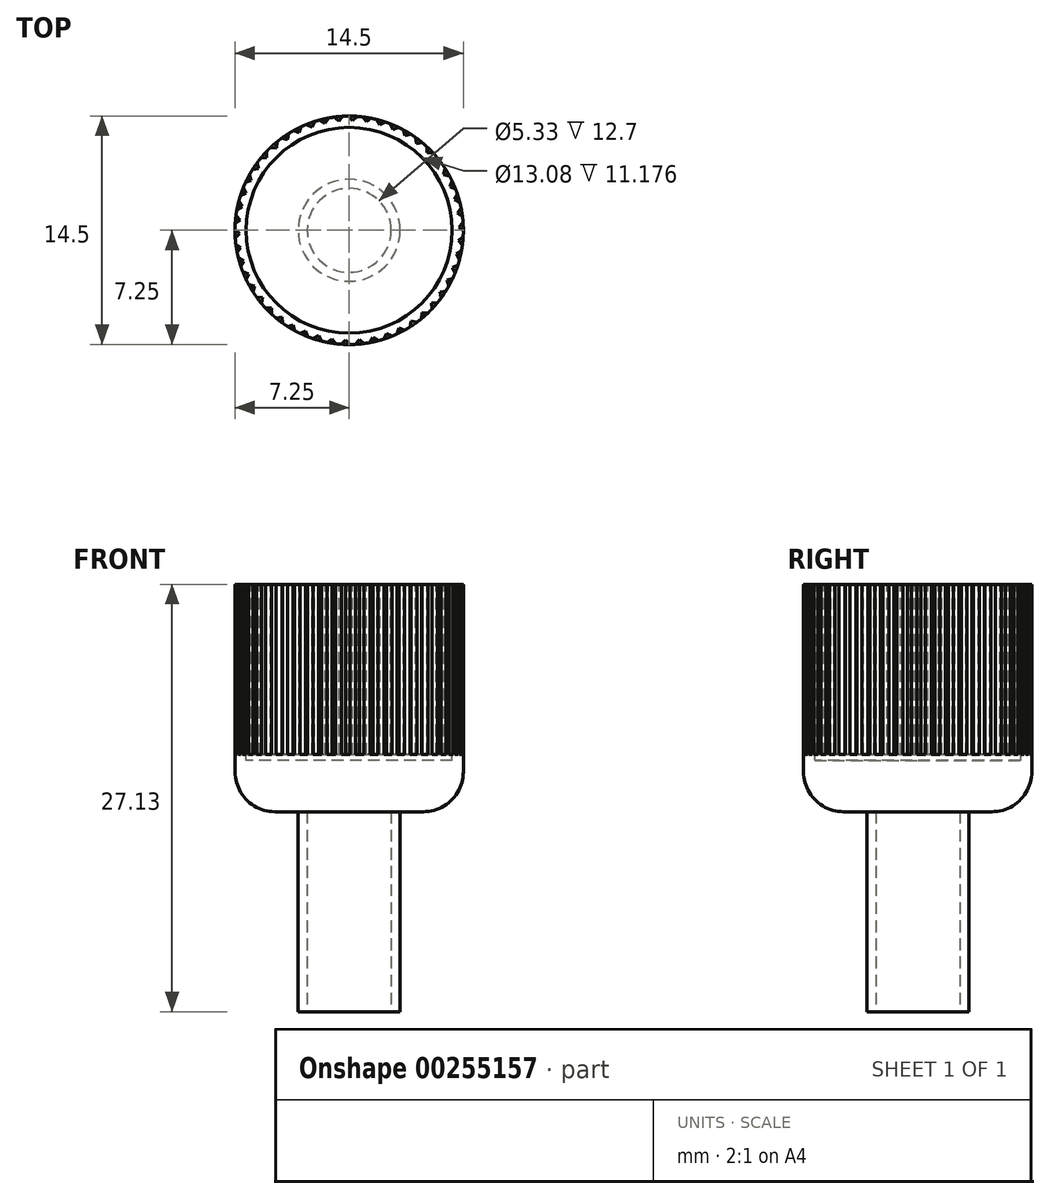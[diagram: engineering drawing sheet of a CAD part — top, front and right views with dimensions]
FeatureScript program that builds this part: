
annotation { "Feature Type Name" : "Feature", "Feature Type Description" : "" }
export const myFeature = defineFeature(function(context is Context, id is Id, definition is map)
    precondition{}
    {
        {
            var Q0;
            Q0=qCreatedBy(makeId("Top.planeOp"),FACE);
            var sketch = newSketch(context, id + "F0", { "sketchPlane" : qUnion([Q0])});
            skCircle(sketch, "E0", {"center": v(0, 0) * mm, "radius": 3.24 * mm});
            skCircle(sketch, "E1", {"center": v(0, 0) * mm, "radius": 2.67 * mm});
            skSolve(sketch);
        }
        {
            var Q0;
            Q0=makeQuery(id+"F0.imprint","IMPRINT",FACE,{"disambiguationData":[TD([[makeQuery(id+"F0.imprint","IMPRINT",EDGE,{"derivedFrom":sQuery(id+"F0.wireOp",EDGE,"E0")}),1.0]])]});
            extrude(context, id + "F1", {"entities" : qUnion([Q0]), "depth" : 12.7 * mm});
        }
        {
            var Q0;
            Q0=makeQuery(id+"F1.opExtrude","CAP_FACE",FACE,{"disambiguationData":[OSD([sQuery(id+"F0.wireOp",EDGE,"E0"),sQuery(id+"F0.wireOp",EDGE,"E1")])],"isStart":false});
            var sketch = newSketch(context, id + "F2", { "sketchPlane" : qUnion([Q0])});
            skCircle(sketch, "E2", {"center": v(0, 0) * mm, "radius": 7.25 * mm});
            skSolve(sketch);
        }
        {
            var Q0;
            Q0 = qSketchRegion(id + "F2", true);
            extrude(context, id + "F3", {"entities" : qUnion([Q0]), "operationType" : NewBodyOperationType.ADD, "depth" : 14.43 * mm});
        }
        {
            var Q0;
            Q0=makeQuery(id+"F3.opExtrude","CAP_EDGE",EDGE,{"disambiguationData":[OSD([sQuery(id+"F2.wireOp",EDGE,"E2")])],"isStart":true});
            fillet(context, id + "F4", {"entities" : qUnion([Q0]), "radius" : 2.54 * mm, "tangentPropagation" : true, "allowEdgeOverflow" : false});
        }
        {
            var Q0;
            Q0=makeQuery(id+"F3.opExtrude","CAP_FACE",FACE,{"disambiguationData":[OSD([sQuery(id+"F2.wireOp",EDGE,"E2")])],"isStart":false});
            var sketch = newSketch(context, id + "F5", { "sketchPlane" : qUnion([Q0])});
            skCircle(sketch, "E3", {"center": v(0, 0) * mm, "radius": 6.54 * mm});
            skSolve(sketch);
        }
        {
            var Q0;
            Q0=makeQuery(id+"F5.imprint","IMPRINT",FACE,{"disambiguationData":[TD([[makeQuery(id+"F5.imprint","IMPRINT",EDGE,{"derivedFrom":sQuery(id+"F5.wireOp",EDGE,"E3")}),1.0]])]});
            extrude(context, id + "F6", {"entities" : qUnion([Q0]), "operationType" : NewBodyOperationType.REMOVE, "oppositeDirection" : true, "depth" : 11.18 * mm});
        }
        {
            var Q0;
            Q0=makeQuery(id+"F3.opExtrude","CAP_FACE",FACE,{"disambiguationData":[OSD([sQuery(id+"F2.wireOp",EDGE,"E2")])],"isStart":false});
            var sketch = newSketch(context, id + "F7", { "sketchPlane" : qUnion([Q0])});
            skLineSegment(sketch, "E4", {"start": v(4.93, 5.31) * mm, "end": v(4.93, 4.93) * mm});
            skLineSegment(sketch, "E5", {"start": v(4.93, 4.93) * mm, "end": v(5.31, 4.93) * mm});
            skArc(sketch, "E6.0", {"start": v(5.9, 4.23) * mm, "mid": v(5.44, 4.8) * mm, "end": v(4.93, 5.31) * mm});
            skLineSegment(sketch, "E7.1.0", {"start": v(4.23, 5.9) * mm, "end": v(4.28, 5.51) * mm});
            skLineSegment(sketch, "E7.1.1", {"start": v(4.28, 5.51) * mm, "end": v(4.65, 5.56) * mm});
            skLineSegment(sketch, "E7.2.0", {"start": v(3.46, 6.37) * mm, "end": v(3.55, 6) * mm});
            skLineSegment(sketch, "E7.2.1", {"start": v(3.55, 6) * mm, "end": v(3.92, 6.1) * mm});
            skLineSegment(sketch, "E7.3.0", {"start": v(2.63, 6.76) * mm, "end": v(2.77, 6.4) * mm});
            skLineSegment(sketch, "E7.3.1", {"start": v(2.77, 6.4) * mm, "end": v(3.13, 6.54) * mm});
            skLineSegment(sketch, "E7.4.0", {"start": v(1.76, 7.03) * mm, "end": v(1.95, 6.7) * mm});
            skLineSegment(sketch, "E7.4.1", {"start": v(1.95, 6.7) * mm, "end": v(2.28, 6.88) * mm});
            skLineSegment(sketch, "E7.5.0", {"start": v(0.87, 7.2) * mm, "end": v(1.1, 6.9) * mm});
            skLineSegment(sketch, "E7.5.1", {"start": v(1.1, 6.9) * mm, "end": v(1.4, 7.12) * mm});
            skLineSegment(sketch, "E7.6.0", {"start": v(-0.04, 7.25) * mm, "end": v(0.22, 6.97) * mm});
            skLineSegment(sketch, "E7.6.1", {"start": v(0.22, 6.97) * mm, "end": v(0.5, 7.23) * mm});
            skLineSegment(sketch, "E7.7.0", {"start": v(-0.95, 7.19) * mm, "end": v(-0.66, 6.95) * mm});
            skLineSegment(sketch, "E7.7.1", {"start": v(-0.66, 6.95) * mm, "end": v(-0.41, 7.24) * mm});
            skLineSegment(sketch, "E7.8.0", {"start": v(-1.84, 7.01) * mm, "end": v(-1.52, 6.8) * mm});
            skLineSegment(sketch, "E7.8.1", {"start": v(-1.52, 6.8) * mm, "end": v(-1.32, 7.13) * mm});
            skLineSegment(sketch, "E7.9.0", {"start": v(-2.7, 6.73) * mm, "end": v(-2.36, 6.56) * mm});
            skLineSegment(sketch, "E7.9.1", {"start": v(-2.36, 6.56) * mm, "end": v(-2.2, 6.9) * mm});
            skLineSegment(sketch, "E7.10.0", {"start": v(-3.53, 6.33) * mm, "end": v(-3.17, 6.22) * mm});
            skLineSegment(sketch, "E7.10.1", {"start": v(-3.17, 6.22) * mm, "end": v(-3.05, 6.58) * mm});
            skLineSegment(sketch, "E7.11.0", {"start": v(-4.3, 5.84) * mm, "end": v(-3.92, 5.77) * mm});
            skLineSegment(sketch, "E7.11.1", {"start": v(-3.92, 5.77) * mm, "end": v(-3.85, 6.15) * mm});
            skLineSegment(sketch, "E7.12.0", {"start": v(-5, 5.26) * mm, "end": v(-4.61, 5.23) * mm});
            skLineSegment(sketch, "E7.12.1", {"start": v(-4.61, 5.23) * mm, "end": v(-4.6, 5.61) * mm});
            skLineSegment(sketch, "E7.13.0", {"start": v(-5.61, 4.6) * mm, "end": v(-5.23, 4.61) * mm});
            skLineSegment(sketch, "E7.13.1", {"start": v(-5.23, 4.61) * mm, "end": v(-5.26, 5) * mm});
            skLineSegment(sketch, "E7.14.0", {"start": v(-6.15, 3.85) * mm, "end": v(-5.77, 3.92) * mm});
            skLineSegment(sketch, "E7.14.1", {"start": v(-5.77, 3.92) * mm, "end": v(-5.84, 4.3) * mm});
            skLineSegment(sketch, "E7.15.0", {"start": v(-6.58, 3.05) * mm, "end": v(-6.22, 3.17) * mm});
            skLineSegment(sketch, "E7.15.1", {"start": v(-6.22, 3.17) * mm, "end": v(-6.33, 3.53) * mm});
            skLineSegment(sketch, "E7.16.0", {"start": v(-6.9, 2.2) * mm, "end": v(-6.56, 2.36) * mm});
            skLineSegment(sketch, "E7.16.1", {"start": v(-6.56, 2.36) * mm, "end": v(-6.73, 2.7) * mm});
            skLineSegment(sketch, "E7.17.0", {"start": v(-7.13, 1.32) * mm, "end": v(-6.8, 1.52) * mm});
            skLineSegment(sketch, "E7.17.1", {"start": v(-6.8, 1.52) * mm, "end": v(-7.01, 1.84) * mm});
            skLineSegment(sketch, "E7.18.0", {"start": v(-7.24, 0.41) * mm, "end": v(-6.95, 0.66) * mm});
            skLineSegment(sketch, "E7.18.1", {"start": v(-6.95, 0.66) * mm, "end": v(-7.19, 0.95) * mm});
            skLineSegment(sketch, "E7.19.0", {"start": v(-7.23, -0.5) * mm, "end": v(-6.97, -0.22) * mm});
            skLineSegment(sketch, "E7.19.1", {"start": v(-6.97, -0.22) * mm, "end": v(-7.25, 0.04) * mm});
            skLineSegment(sketch, "E7.20.0", {"start": v(-7.12, -1.4) * mm, "end": v(-6.9, -1.1) * mm});
            skLineSegment(sketch, "E7.20.1", {"start": v(-6.9, -1.1) * mm, "end": v(-7.2, -0.87) * mm});
            skLineSegment(sketch, "E7.21.0", {"start": v(-6.88, -2.28) * mm, "end": v(-6.7, -1.95) * mm});
            skLineSegment(sketch, "E7.21.1", {"start": v(-6.7, -1.95) * mm, "end": v(-7.03, -1.76) * mm});
            skLineSegment(sketch, "E7.22.0", {"start": v(-6.54, -3.13) * mm, "end": v(-6.4, -2.77) * mm});
            skLineSegment(sketch, "E7.22.1", {"start": v(-6.4, -2.77) * mm, "end": v(-6.76, -2.63) * mm});
            skLineSegment(sketch, "E7.23.0", {"start": v(-6.1, -3.92) * mm, "end": v(-6, -3.55) * mm});
            skLineSegment(sketch, "E7.23.1", {"start": v(-6, -3.55) * mm, "end": v(-6.37, -3.46) * mm});
            skLineSegment(sketch, "E7.24.0", {"start": v(-5.56, -4.65) * mm, "end": v(-5.51, -4.28) * mm});
            skLineSegment(sketch, "E7.24.1", {"start": v(-5.51, -4.28) * mm, "end": v(-5.9, -4.23) * mm});
            skLineSegment(sketch, "E7.25.0", {"start": v(-4.93, -5.31) * mm, "end": v(-4.93, -4.93) * mm});
            skLineSegment(sketch, "E7.25.1", {"start": v(-4.93, -4.93) * mm, "end": v(-5.31, -4.93) * mm});
            skLineSegment(sketch, "E7.26.0", {"start": v(-4.23, -5.9) * mm, "end": v(-4.28, -5.51) * mm});
            skLineSegment(sketch, "E7.26.1", {"start": v(-4.28, -5.51) * mm, "end": v(-4.65, -5.56) * mm});
            skLineSegment(sketch, "E7.27.0", {"start": v(-3.46, -6.37) * mm, "end": v(-3.55, -6) * mm});
            skLineSegment(sketch, "E7.27.1", {"start": v(-3.55, -6) * mm, "end": v(-3.92, -6.1) * mm});
            skLineSegment(sketch, "E7.28.0", {"start": v(-2.63, -6.76) * mm, "end": v(-2.77, -6.4) * mm});
            skLineSegment(sketch, "E7.28.1", {"start": v(-2.77, -6.4) * mm, "end": v(-3.13, -6.54) * mm});
            skLineSegment(sketch, "E7.29.0", {"start": v(-1.76, -7.03) * mm, "end": v(-1.95, -6.7) * mm});
            skLineSegment(sketch, "E7.29.1", {"start": v(-1.95, -6.7) * mm, "end": v(-2.28, -6.88) * mm});
            skLineSegment(sketch, "E7.30.0", {"start": v(-0.87, -7.2) * mm, "end": v(-1.1, -6.9) * mm});
            skLineSegment(sketch, "E7.30.1", {"start": v(-1.1, -6.9) * mm, "end": v(-1.4, -7.12) * mm});
            skLineSegment(sketch, "E7.31.0", {"start": v(0.04, -7.25) * mm, "end": v(-0.22, -6.97) * mm});
            skLineSegment(sketch, "E7.31.1", {"start": v(-0.22, -6.97) * mm, "end": v(-0.5, -7.23) * mm});
            skLineSegment(sketch, "E7.32.0", {"start": v(0.95, -7.19) * mm, "end": v(0.66, -6.95) * mm});
            skLineSegment(sketch, "E7.32.1", {"start": v(0.66, -6.95) * mm, "end": v(0.41, -7.24) * mm});
            skLineSegment(sketch, "E7.33.0", {"start": v(1.84, -7.01) * mm, "end": v(1.52, -6.8) * mm});
            skLineSegment(sketch, "E7.33.1", {"start": v(1.52, -6.8) * mm, "end": v(1.32, -7.13) * mm});
            skLineSegment(sketch, "E7.34.0", {"start": v(2.7, -6.73) * mm, "end": v(2.36, -6.56) * mm});
            skLineSegment(sketch, "E7.34.1", {"start": v(2.36, -6.56) * mm, "end": v(2.2, -6.9) * mm});
            skLineSegment(sketch, "E7.35.0", {"start": v(3.53, -6.33) * mm, "end": v(3.17, -6.22) * mm});
            skLineSegment(sketch, "E7.35.1", {"start": v(3.17, -6.22) * mm, "end": v(3.05, -6.58) * mm});
            skLineSegment(sketch, "E7.36.0", {"start": v(4.3, -5.84) * mm, "end": v(3.92, -5.77) * mm});
            skLineSegment(sketch, "E7.36.1", {"start": v(3.92, -5.77) * mm, "end": v(3.85, -6.15) * mm});
            skLineSegment(sketch, "E7.37.0", {"start": v(5, -5.26) * mm, "end": v(4.61, -5.23) * mm});
            skLineSegment(sketch, "E7.37.1", {"start": v(4.61, -5.23) * mm, "end": v(4.6, -5.61) * mm});
            skLineSegment(sketch, "E7.38.0", {"start": v(5.61, -4.6) * mm, "end": v(5.23, -4.61) * mm});
            skLineSegment(sketch, "E7.38.1", {"start": v(5.23, -4.61) * mm, "end": v(5.26, -5) * mm});
            skLineSegment(sketch, "E7.39.0", {"start": v(6.15, -3.85) * mm, "end": v(5.77, -3.92) * mm});
            skLineSegment(sketch, "E7.39.1", {"start": v(5.77, -3.92) * mm, "end": v(5.84, -4.3) * mm});
            skLineSegment(sketch, "E7.40.0", {"start": v(6.58, -3.05) * mm, "end": v(6.22, -3.17) * mm});
            skLineSegment(sketch, "E7.40.1", {"start": v(6.22, -3.17) * mm, "end": v(6.33, -3.53) * mm});
            skLineSegment(sketch, "E7.41.0", {"start": v(6.9, -2.2) * mm, "end": v(6.56, -2.36) * mm});
            skLineSegment(sketch, "E7.41.1", {"start": v(6.56, -2.36) * mm, "end": v(6.73, -2.7) * mm});
            skLineSegment(sketch, "E7.42.0", {"start": v(7.13, -1.32) * mm, "end": v(6.8, -1.52) * mm});
            skLineSegment(sketch, "E7.42.1", {"start": v(6.8, -1.52) * mm, "end": v(7.01, -1.84) * mm});
            skLineSegment(sketch, "E7.43.0", {"start": v(7.24, -0.41) * mm, "end": v(6.95, -0.66) * mm});
            skLineSegment(sketch, "E7.43.1", {"start": v(6.95, -0.66) * mm, "end": v(7.19, -0.95) * mm});
            skLineSegment(sketch, "E7.44.0", {"start": v(7.23, 0.5) * mm, "end": v(6.97, 0.22) * mm});
            skLineSegment(sketch, "E7.44.1", {"start": v(6.97, 0.22) * mm, "end": v(7.25, -0.04) * mm});
            skLineSegment(sketch, "E7.45.0", {"start": v(7.12, 1.4) * mm, "end": v(6.9, 1.1) * mm});
            skLineSegment(sketch, "E7.45.1", {"start": v(6.9, 1.1) * mm, "end": v(7.2, 0.87) * mm});
            skLineSegment(sketch, "E7.46.0", {"start": v(6.88, 2.28) * mm, "end": v(6.7, 1.95) * mm});
            skLineSegment(sketch, "E7.46.1", {"start": v(6.7, 1.95) * mm, "end": v(7.03, 1.76) * mm});
            skLineSegment(sketch, "E7.47.0", {"start": v(6.54, 3.13) * mm, "end": v(6.4, 2.77) * mm});
            skLineSegment(sketch, "E7.47.1", {"start": v(6.4, 2.77) * mm, "end": v(6.76, 2.63) * mm});
            skLineSegment(sketch, "E7.48.0", {"start": v(6.1, 3.92) * mm, "end": v(6, 3.55) * mm});
            skLineSegment(sketch, "E7.48.1", {"start": v(6, 3.55) * mm, "end": v(6.37, 3.46) * mm});
            skLineSegment(sketch, "E7.49.0", {"start": v(5.56, 4.65) * mm, "end": v(5.51, 4.28) * mm});
            skLineSegment(sketch, "E7.49.1", {"start": v(5.51, 4.28) * mm, "end": v(5.9, 4.23) * mm});
            skArc(sketch, "E8.trimOffspring", {"start": v(6.37, 3.46) * mm, "mid": v(6.24, 3.7) * mm, "end": v(6.1, 3.92) * mm});
            skArc(sketch, "E9.trimOffspring", {"start": v(6.76, 2.63) * mm, "mid": v(6.66, 2.88) * mm, "end": v(6.54, 3.13) * mm});
            skArc(sketch, "E10.trimOffspring", {"start": v(7.03, 1.76) * mm, "mid": v(6.96, 2.02) * mm, "end": v(6.88, 2.28) * mm});
            skArc(sketch, "E11.trimOffspring", {"start": v(7.2, 0.87) * mm, "mid": v(7.16, 1.13) * mm, "end": v(7.12, 1.4) * mm});
            skArc(sketch, "E12.trimOffspring", {"start": v(7.25, -0.04) * mm, "mid": v(7.25, 0.23) * mm, "end": v(7.23, 0.5) * mm});
            skArc(sketch, "E13.trimOffspring", {"start": v(7.19, -0.95) * mm, "mid": v(7.22, -0.68) * mm, "end": v(7.24, -0.41) * mm});
            skArc(sketch, "E14.trimOffspring", {"start": v(7.01, -1.84) * mm, "mid": v(7.08, -1.58) * mm, "end": v(7.13, -1.32) * mm});
            skArc(sketch, "E15.trimOffspring", {"start": v(6.73, -2.7) * mm, "mid": v(6.82, -2.46) * mm, "end": v(6.9, -2.2) * mm});
            skArc(sketch, "E16.trimOffspring", {"start": v(6.33, -3.53) * mm, "mid": v(6.46, -3.3) * mm, "end": v(6.58, -3.05) * mm});
            skArc(sketch, "E17.trimOffspring", {"start": v(5.84, -4.3) * mm, "mid": v(6, -4.08) * mm, "end": v(6.15, -3.85) * mm});
            skArc(sketch, "E18.trimOffspring", {"start": v(5.26, -5) * mm, "mid": v(5.44, -4.8) * mm, "end": v(5.61, -4.6) * mm});
            skArc(sketch, "E19.trimOffspring", {"start": v(4.6, -5.61) * mm, "mid": v(4.8, -5.44) * mm, "end": v(5, -5.26) * mm});
            skArc(sketch, "E20.trimOffspring", {"start": v(3.85, -6.15) * mm, "mid": v(4.08, -6) * mm, "end": v(4.3, -5.84) * mm});
            skArc(sketch, "E21.trimOffspring", {"start": v(3.05, -6.58) * mm, "mid": v(3.3, -6.46) * mm, "end": v(3.53, -6.33) * mm});
            skArc(sketch, "E22.trimOffspring", {"start": v(2.2, -6.9) * mm, "mid": v(2.46, -6.82) * mm, "end": v(2.7, -6.73) * mm});
            skArc(sketch, "E23.trimOffspring", {"start": v(1.32, -7.13) * mm, "mid": v(1.58, -7.08) * mm, "end": v(1.84, -7.01) * mm});
            skArc(sketch, "E24.trimOffspring", {"start": v(0.41, -7.24) * mm, "mid": v(0.68, -7.22) * mm, "end": v(0.95, -7.19) * mm});
            skArc(sketch, "E25.trimOffspring", {"start": v(-0.5, -7.23) * mm, "mid": v(-0.23, -7.25) * mm, "end": v(0.04, -7.25) * mm});
            skArc(sketch, "E26.trimOffspring", {"start": v(-1.4, -7.12) * mm, "mid": v(-1.13, -7.16) * mm, "end": v(-0.87, -7.2) * mm});
            skArc(sketch, "E27.trimOffspring", {"start": v(-2.28, -6.88) * mm, "mid": v(-2.02, -6.96) * mm, "end": v(-1.76, -7.03) * mm});
            skArc(sketch, "E28.trimOffspring", {"start": v(-3.13, -6.54) * mm, "mid": v(-2.88, -6.66) * mm, "end": v(-2.63, -6.76) * mm});
            skArc(sketch, "E29.trimOffspring", {"start": v(-3.92, -6.1) * mm, "mid": v(-3.7, -6.24) * mm, "end": v(-3.46, -6.37) * mm});
            skArc(sketch, "E30.trimOffspring", {"start": v(-4.65, -5.56) * mm, "mid": v(-4.44, -5.73) * mm, "end": v(-4.23, -5.9) * mm});
            skArc(sketch, "E31.trimOffspring", {"start": v(-5.31, -4.93) * mm, "mid": v(-5.13, -5.13) * mm, "end": v(-4.93, -5.31) * mm});
            skArc(sketch, "E32.trimOffspring", {"start": v(-5.9, -4.23) * mm, "mid": v(-5.73, -4.44) * mm, "end": v(-5.56, -4.65) * mm});
            skArc(sketch, "E33.trimOffspring", {"start": v(-6.37, -3.46) * mm, "mid": v(-6.24, -3.7) * mm, "end": v(-6.1, -3.92) * mm});
            skArc(sketch, "E34.trimOffspring", {"start": v(-6.76, -2.63) * mm, "mid": v(-6.66, -2.88) * mm, "end": v(-6.54, -3.13) * mm});
            skArc(sketch, "E35.trimOffspring", {"start": v(-7.03, -1.76) * mm, "mid": v(-6.96, -2.02) * mm, "end": v(-6.88, -2.28) * mm});
            skArc(sketch, "E36.trimOffspring", {"start": v(-7.2, -0.87) * mm, "mid": v(-7.16, -1.13) * mm, "end": v(-7.12, -1.4) * mm});
            skArc(sketch, "E37.trimOffspring", {"start": v(-7.25, 0.04) * mm, "mid": v(-7.25, -0.23) * mm, "end": v(-7.23, -0.5) * mm});
            skArc(sketch, "E38.trimOffspring", {"start": v(-7.19, 0.95) * mm, "mid": v(-7.22, 0.68) * mm, "end": v(-7.24, 0.41) * mm});
            skArc(sketch, "E39.trimOffspring", {"start": v(-7.01, 1.84) * mm, "mid": v(-7.08, 1.58) * mm, "end": v(-7.13, 1.32) * mm});
            skArc(sketch, "E40.trimOffspring", {"start": v(-6.73, 2.7) * mm, "mid": v(-6.82, 2.46) * mm, "end": v(-6.9, 2.2) * mm});
            skArc(sketch, "E41.trimOffspring", {"start": v(-6.33, 3.53) * mm, "mid": v(-6.46, 3.3) * mm, "end": v(-6.58, 3.05) * mm});
            skArc(sketch, "E42.trimOffspring", {"start": v(-5.84, 4.3) * mm, "mid": v(-6, 4.08) * mm, "end": v(-6.15, 3.85) * mm});
            skArc(sketch, "E43.trimOffspring", {"start": v(-5.26, 5) * mm, "mid": v(-5.44, 4.8) * mm, "end": v(-5.61, 4.6) * mm});
            skArc(sketch, "E44.trimOffspring", {"start": v(-4.6, 5.61) * mm, "mid": v(-4.8, 5.44) * mm, "end": v(-5, 5.26) * mm});
            skArc(sketch, "E45.trimOffspring", {"start": v(-3.85, 6.15) * mm, "mid": v(-4.08, 6) * mm, "end": v(-4.3, 5.84) * mm});
            skArc(sketch, "E46.trimOffspring", {"start": v(-3.05, 6.58) * mm, "mid": v(-3.3, 6.46) * mm, "end": v(-3.53, 6.33) * mm});
            skArc(sketch, "E47.trimOffspring", {"start": v(-2.2, 6.9) * mm, "mid": v(-2.46, 6.82) * mm, "end": v(-2.7, 6.73) * mm});
            skArc(sketch, "E48.trimOffspring", {"start": v(-1.32, 7.13) * mm, "mid": v(-1.58, 7.08) * mm, "end": v(-1.84, 7.01) * mm});
            skArc(sketch, "E49.trimOffspring", {"start": v(-0.41, 7.24) * mm, "mid": v(-0.68, 7.22) * mm, "end": v(-0.95, 7.19) * mm});
            skArc(sketch, "E50.trimOffspring", {"start": v(0.5, 7.23) * mm, "mid": v(0.23, 7.25) * mm, "end": v(-0.04, 7.25) * mm});
            skArc(sketch, "E51.trimOffspring", {"start": v(1.4, 7.12) * mm, "mid": v(1.13, 7.16) * mm, "end": v(0.87, 7.2) * mm});
            skArc(sketch, "E52.trimOffspring", {"start": v(2.28, 6.88) * mm, "mid": v(2.02, 6.96) * mm, "end": v(1.76, 7.03) * mm});
            skArc(sketch, "E53.trimOffspring", {"start": v(3.13, 6.54) * mm, "mid": v(2.88, 6.66) * mm, "end": v(2.63, 6.76) * mm});
            skArc(sketch, "E54.trimOffspring", {"start": v(3.92, 6.1) * mm, "mid": v(3.7, 6.24) * mm, "end": v(3.46, 6.37) * mm});
            skArc(sketch, "E55.trimOffspring", {"start": v(4.65, 5.56) * mm, "mid": v(4.44, 5.73) * mm, "end": v(4.23, 5.9) * mm});
            skSolve(sketch);
        }
        {
            var Q0;
            Q0 = qSketchRegion(id + "F7", true);
            extrude(context, id + "F8", {"entities" : qUnion([Q0]), "operationType" : NewBodyOperationType.REMOVE, "oppositeDirection" : true, "depth" : 10.8 * mm});
        }
    });
